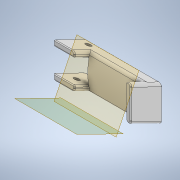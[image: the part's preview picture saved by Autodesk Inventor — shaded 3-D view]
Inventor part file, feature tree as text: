
AUTODESK INVENTOR PART (.ipt)
format: ipt  version: 2020 (Build 240168000, 168)  size: 287,232 bytes
history: native  units: in
note: dims shown in document units (in); Inventor stores cm internally (conversion verified against a paired STEP export)
features: extrude x5, sketch x5, plane x2, fillet x2, chamfer x1
ambient origin geometry x8: Origin, YZ Plane, XZ Plane, XY Plane, X Axis, Y Axis, Z Axis, Center Point
bodies: Solid1 (feature_tree)
feature tree (15):
  extrude  "Extrusion1"  Depth=3.6875in
  plane  "Work Plane2"
  extrude  "Extrusion2"  Depth=0.4391in
  extrude  "Extrusion3"  Depth=1.0157in
  extrude  "Extrusion4"  Depth=0.25in
  extrude  "Extrusion5"  TaperAngle=0.0deg  [1 undecoded]
  fillet  "Fillet1"  Radius=0.2656in
  fillet  "Fillet2"  Radius=0.375in
  chamfer  "Chamfer1"  Distance=0.5in
  sketch  "Sketch1"  dims[d0=2.5in d1=3.6875in]
  plane  "Work Plane1"
  sketch  "Sketch2"  dims[d2=1.5in d3=0.0in d4=0.4391in]
  sketch  "Sketch3"  dims[d5=90.0deg d6=1.0157in]
  sketch  "Sketch4"  dims[d7=0.25in d8=0.25in]
  sketch  "Sketch5"  dims[d9=1.0in d10=0.0in d11=0.0in d12=0.2656in d13=0.375in d14=0.5in d15=0.0in d16=0.0in d17=2.4375in d18=0.75in d19=0.0in d20=3.0in d21=1.25in d22=0.0in d23=0.125in d24=0.125in d25=0.0625in d26=0.05in d27=0.125in d28=45.0deg d29=0.5in d30=0.0344in d31=0.5in d32=0.0344in]
note: 1 required parameter value undecoded (feature->parameter linkage not recoverable at this tier; creation-order binding heuristic only, values carry confidence <= 0.55)
